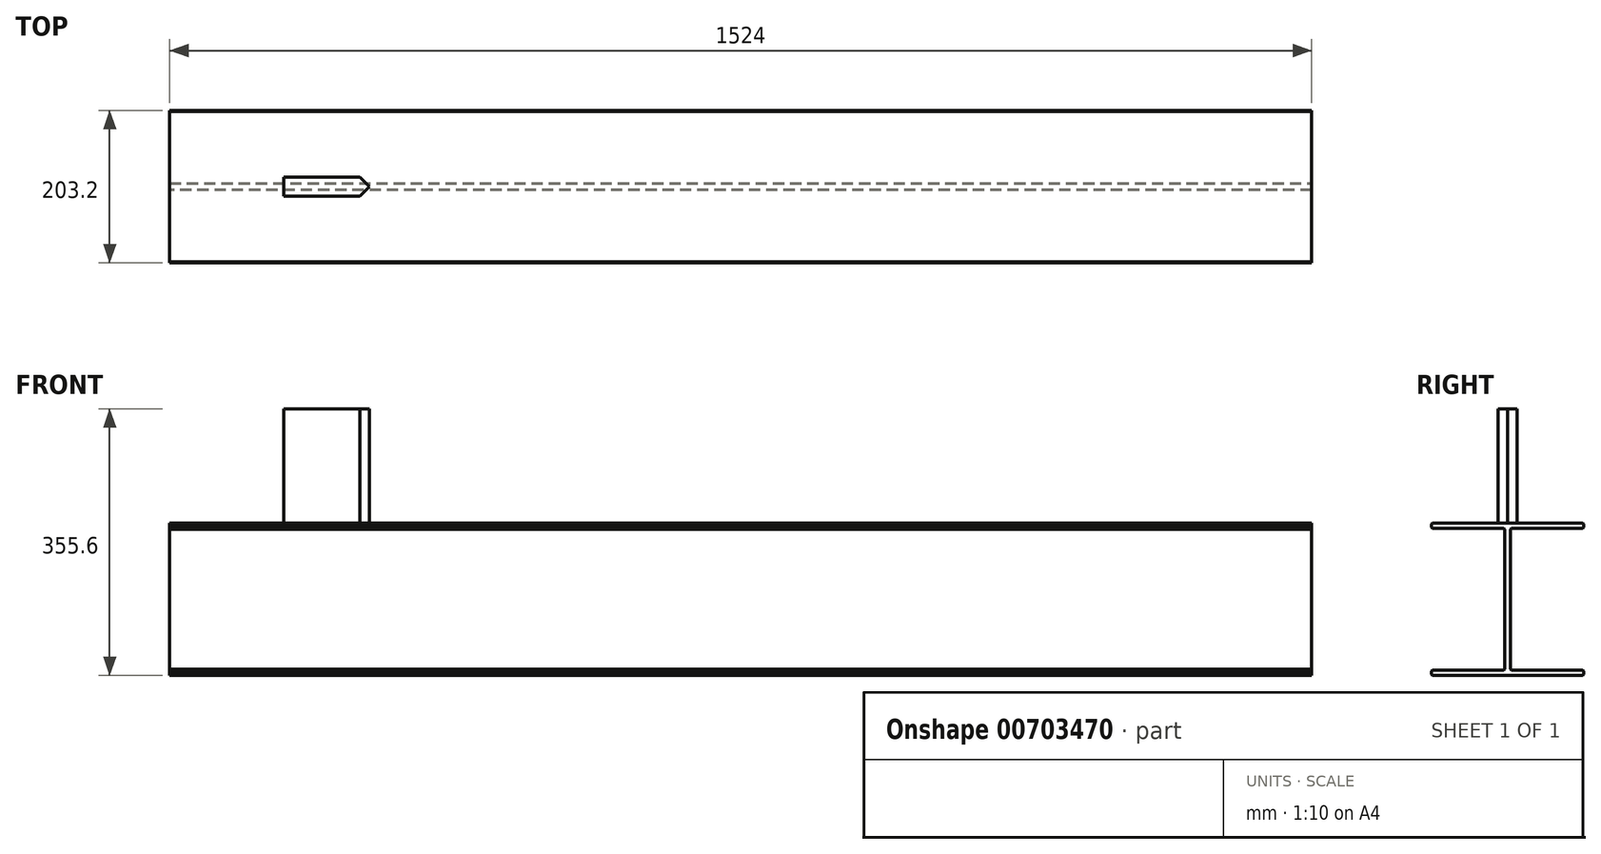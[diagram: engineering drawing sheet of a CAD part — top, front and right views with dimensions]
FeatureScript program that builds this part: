
annotation { "Feature Type Name" : "Feature", "Feature Type Description" : "" }
export const myFeature = defineFeature(function(context is Context, id is Id, definition is map)
    precondition{}
    {
        {
            var Q0;
            Q0=qCreatedBy(makeId("Right.planeOp"),FACE);
            var sketch = newSketch(context, id + "F0", { "sketchPlane" : qUnion([Q0])});
            skLineSegment(sketch, "E0.bottom", {"start": v(-101.6, 101.6) * mm, "end": v(101.6, 101.6) * mm});
            skLineSegment(sketch, "E0.top", {"start": v(-101.6, -101.6) * mm, "end": v(101.6, -101.6) * mm});
            skLineSegment(sketch, "E0.left", {"start": v(-101.6, 101.6) * mm, "end": v(-101.6, 94.36) * mm});
            skLineSegment(sketch, "E0.right", {"start": v(101.6, 101.6) * mm, "end": v(101.6, 94.36) * mm});
            skLineSegment(sketch, "E1.0", {"start": v(-101.6, 94.36) * mm, "end": v(-3.62, 94.36) * mm});
            skLineSegment(sketch, "E2.0", {"start": v(-101.6, -94.36) * mm, "end": v(-3.62, -94.36) * mm});
            skLineSegment(sketch, "E3.0", {"start": v(3.62, -94.36) * mm, "end": v(3.62, 94.36) * mm});
            skLineSegment(sketch, "E4.0", {"start": v(-3.62, -94.36) * mm, "end": v(-3.62, 94.36) * mm});
            skPoint(sketch, "E5.end.orphan", {"position": v(0, 94.36) * mm});
            skPoint(sketch, "E5.start.orphan", {"position": v(0, -94.36) * mm});
            skLineSegment(sketch, "E6.trimOffspring", {"start": v(3.62, 94.36) * mm, "end": v(101.6, 94.36) * mm});
            skLineSegment(sketch, "E7.trimOffspring", {"start": v(3.62, -94.36) * mm, "end": v(101.6, -94.36) * mm});
            skLineSegment(sketch, "E8.trimOffspring", {"start": v(-101.6, -94.36) * mm, "end": v(-101.6, -101.6) * mm});
            skLineSegment(sketch, "E9.trimOffspring", {"start": v(101.6, -94.36) * mm, "end": v(101.6, -101.6) * mm});
            skLineSegment(sketch, "E10", {"start": v(0, 0) * mm, "end": v(3.62, 0) * mm});
            skLineSegment(sketch, "E11", {"start": v(3.62, 0) * mm, "end": v(0, 0) * mm});
            skLineSegment(sketch, "E12", {"start": v(-3.62, 0) * mm, "end": v(0, 0) * mm});
            skSolve(sketch);
        }
        {
            var Q0;
            Q0 = qSketchRegion(id + "F0", true);
            extrude(context, id + "F1", {"entities" : qUnion([Q0]), "depth" : 1524 * mm, "offsetDistance" : 25.4 * mm});
        }
        {
            var Q0;
            Q0=makeQuery(id+"F1.opExtrude","SWEPT_EDGE",EDGE,{"disambiguationData":[OSD([sQuery(id+"F0.wireOp",EDGE,"E0.bottom"),sQuery(id+"F0.wireOp",EDGE,"E0.left")])]});
            var Q1;
            Q1=makeQuery(id+"F1.opExtrude","SWEPT_EDGE",EDGE,{"disambiguationData":[OSD([sQuery(id+"F0.wireOp",EDGE,"E0.left"),sQuery(id+"F0.wireOp",EDGE,"E1.0")])]});
            var Q2;
            Q2=makeQuery(id+"F1.opExtrude","SWEPT_EDGE",EDGE,{"disambiguationData":[OSD([sQuery(id+"F0.wireOp",EDGE,"E0.bottom"),sQuery(id+"F0.wireOp",EDGE,"E0.right")])]});
            var Q3;
            Q3=makeQuery(id+"F1.opExtrude","SWEPT_EDGE",EDGE,{"disambiguationData":[OSD([sQuery(id+"F0.wireOp",EDGE,"E0.right"),sQuery(id+"F0.wireOp",EDGE,"E6.trimOffspring")])]});
            var Q4;
            Q4=makeQuery(id+"F1.opExtrude","SWEPT_EDGE",EDGE,{"disambiguationData":[OSD([sQuery(id+"F0.wireOp",EDGE,"E7.trimOffspring"),sQuery(id+"F0.wireOp",EDGE,"E9.trimOffspring")])]});
            var Q5;
            Q5=makeQuery(id+"F1.opExtrude","SWEPT_EDGE",EDGE,{"disambiguationData":[OSD([sQuery(id+"F0.wireOp",EDGE,"E0.top"),sQuery(id+"F0.wireOp",EDGE,"E9.trimOffspring")])]});
            var Q6;
            Q6=makeQuery(id+"F1.opExtrude","SWEPT_EDGE",EDGE,{"disambiguationData":[OSD([sQuery(id+"F0.wireOp",EDGE,"E2.0"),sQuery(id+"F0.wireOp",EDGE,"E8.trimOffspring")])]});
            var Q7;
            Q7=makeQuery(id+"F1.opExtrude","SWEPT_EDGE",EDGE,{"disambiguationData":[OSD([sQuery(id+"F0.wireOp",EDGE,"E0.top"),sQuery(id+"F0.wireOp",EDGE,"E8.trimOffspring")])]});
            chamfer(context, id + "F2", {"entities" : qUnion([Q0, Q1, Q2, Q3, Q4, Q5, Q6, Q7]), "width" : 1.27 * mm, "tangentPropagation" : true});
        }
        {
            var Q0;
            Q0=makeQuery(id+"F1.opExtrude","SWEPT_EDGE",EDGE,{"disambiguationData":[OSD([sQuery(id+"F0.wireOp",EDGE,"E1.0"),sQuery(id+"F0.wireOp",EDGE,"E4.0")])]});
            var Q1;
            Q1=makeQuery(id+"F1.opExtrude","SWEPT_EDGE",EDGE,{"disambiguationData":[OSD([sQuery(id+"F0.wireOp",EDGE,"E3.0"),sQuery(id+"F0.wireOp",EDGE,"E6.trimOffspring")])]});
            var Q2;
            Q2=makeQuery(id+"F1.opExtrude","SWEPT_EDGE",EDGE,{"disambiguationData":[OSD([sQuery(id+"F0.wireOp",EDGE,"E3.0"),sQuery(id+"F0.wireOp",EDGE,"E7.trimOffspring")])]});
            var Q3;
            Q3=makeQuery(id+"F1.opExtrude","SWEPT_EDGE",EDGE,{"disambiguationData":[OSD([sQuery(id+"F0.wireOp",EDGE,"E2.0"),sQuery(id+"F0.wireOp",EDGE,"E4.0")])]});
            chamfer(context, id + "F3", {"entities" : qUnion([Q0, Q1, Q2, Q3]), "width" : 1.27 * mm, "tangentPropagation" : true});
        }
        {
            var Q0;
            Q0=makeQuery(id+"F1.opExtrude","SWEPT_FACE",FACE,{"disambiguationData":[OSD([sQuery(id+"F0.wireOp",EDGE,"E0.bottom")])]});
            var sketch = newSketch(context, id + "F4", { "sketchPlane" : qUnion([Q0])});
            skLineSegment(sketch, "E13.0", {"start": v(152.4, -12.7) * mm, "end": v(254, -12.7) * mm});
            skLineSegment(sketch, "E14.0", {"start": v(152.4, 12.7) * mm, "end": v(254, 12.7) * mm});
            skPoint(sketch, "E15.start.orphan", {"position": v(0, 0) * mm});
            skLineSegment(sketch, "E16", {"start": v(152.4, 12.7) * mm, "end": v(152.4, -12.7) * mm});
            skLineSegment(sketch, "E17", {"start": v(254, -12.7) * mm, "end": v(266.7, 0) * mm});
            skLineSegment(sketch, "E18", {"start": v(254, 12.7) * mm, "end": v(266.7, 0) * mm});
            skSolve(sketch);
        }
        {
            var Q0;
            Q0 = qSketchRegion(id + "F4", true);
            extrude(context, id + "F5", {"entities" : qUnion([Q0]), "operationType" : NewBodyOperationType.ADD, "depth" : 152.4 * mm, "offsetDistance" : 25.4 * mm});
        }
    });
